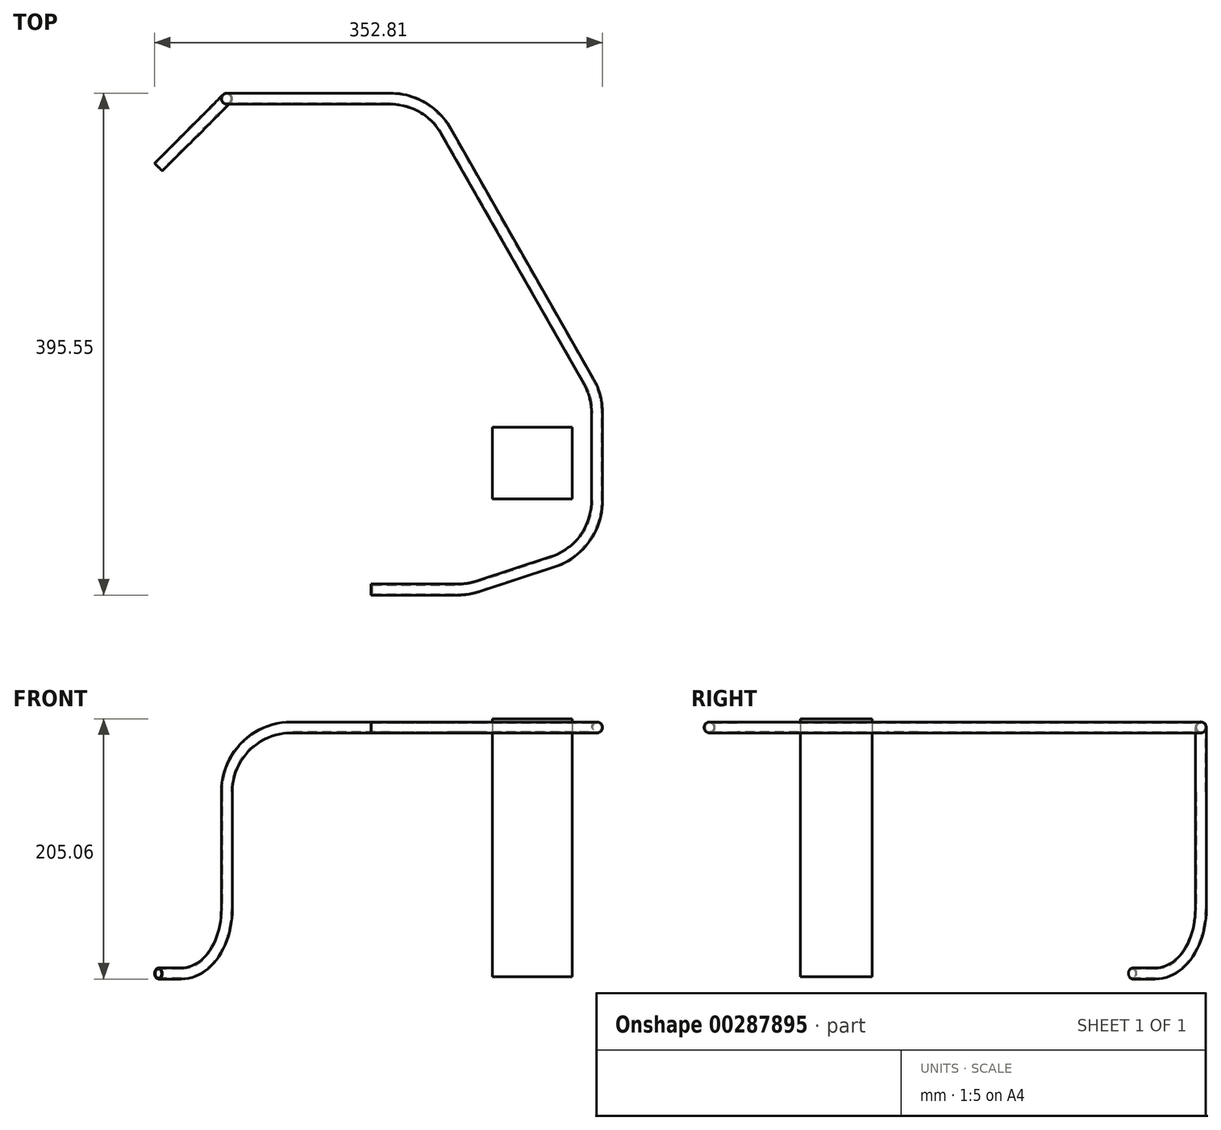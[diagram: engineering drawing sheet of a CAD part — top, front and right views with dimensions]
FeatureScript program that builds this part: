
annotation { "Feature Type Name" : "Feature", "Feature Type Description" : "" }
export const myFeature = defineFeature(function(context is Context, id is Id, definition is map)
    precondition{}
    {
        {
            var Q0;
            Q0=qCreatedBy(makeId("Top.planeOp"),FACE);
            var sketch = newSketch(context, id + "F0", { "sketchPlane" : qUnion([Q0])});
            skLineSegment(sketch, "E0", {"start": v(0, 0) * mm, "end": v(308.08, 0) * mm});
            skLineSegment(sketch, "E1", {"start": v(308.08, 0) * mm, "end": v(308.08, -99.9) * mm});
            skLineSegment(sketch, "E2", {"start": v(308.08, -99.9) * mm, "end": v(333.48, -99.9) * mm});
            skLineSegment(sketch, "E3", {"start": v(0, 0) * mm, "end": v(140.48, 0) * mm});
            skLineSegment(sketch, "E4", {"start": v(140.48, 0) * mm, "end": v(140.48, 233.1) * mm});
            skLineSegment(sketch, "E5", {"start": v(140.48, 233.1) * mm, "end": v(165.88, 233.1) * mm});
            skLineSegment(sketch, "E6", {"start": v(0, 0) * mm, "end": v(466.34, 0) * mm});
            skLineSegment(sketch, "E7", {"start": v(466.34, 0) * mm, "end": v(466.34, -28.43) * mm});
            skLineSegment(sketch, "E8", {"start": v(466.34, -28.43) * mm, "end": v(491.74, -28.43) * mm});
            skLineSegment(sketch, "E9", {"start": v(0, 0) * mm, "end": v(403.6, 0) * mm});
            skLineSegment(sketch, "E10", {"start": v(403.6, 0) * mm, "end": v(403.6, 27.96) * mm});
            skLineSegment(sketch, "E11", {"start": v(403.6, 27.96) * mm, "end": v(429, 27.96) * mm});
            skSolve(sketch);
        }
        {
            var Q0;
            Q0=sQuery(id+"F0.wireOp",EDGE,"E2");
            cPlane(context, id + "F1", {"entities" : qUnion([Q0]), "cplaneType" : CPlaneType.LINE_ANGLE, "offset" : 25.4 * mm, "angle" : 0 * degree, "width" : 152.4 * mm, "height" : 152.4 * mm});
        }
        {
            var Q0;
            Q0=sQuery(id+"F0.wireOp",EDGE,"E8");
            cPlane(context, id + "F2", {"entities" : qUnion([Q0]), "cplaneType" : CPlaneType.LINE_ANGLE, "offset" : 25.4 * mm, "angle" : 0 * degree, "width" : 152.4 * mm, "height" : 152.4 * mm});
        }
        {
            var Q0;
            Q0=sQuery(id+"F0.wireOp",EDGE,"E11");
            cPlane(context, id + "F3", {"entities" : qUnion([Q0]), "cplaneType" : CPlaneType.LINE_ANGLE, "offset" : 25.4 * mm, "angle" : 0 * degree, "width" : 152.4 * mm, "height" : 152.4 * mm});
        }
        {
            var Q0;
            Q0=sQuery(id+"F0.wireOp",EDGE,"E5");
            cPlane(context, id + "F4", {"entities" : qUnion([Q0]), "cplaneType" : CPlaneType.LINE_ANGLE, "offset" : 25.4 * mm, "angle" : 0 * degree, "width" : 152.4 * mm, "height" : 152.4 * mm});
        }
        {
            var Q0;
            Q0=qCreatedBy(id+"F2.planeOp",FACE);
            var sketch = newSketch(context, id + "F5", { "sketchPlane" : qUnion([Q0])});
            skLineSegment(sketch, "E12", {"start": v(-466.34, 0) * mm, "end": v(-466.34, 772.24) * mm});
            skLineSegment(sketch, "E13", {"start": v(-466.34, 772.24) * mm, "end": v(-440.94, 772.24) * mm});
            skSolve(sketch);
        }
        {
            var Q0;
            Q0=qCreatedBy(id+"F3.planeOp",FACE);
            var sketch = newSketch(context, id + "F6", { "sketchPlane" : qUnion([Q0])});
            skLineSegment(sketch, "E14", {"start": v(-403.6, 0) * mm, "end": v(-403.6, 772.24) * mm});
            skLineSegment(sketch, "E15", {"start": v(-403.6, 772.24) * mm, "end": v(-378.2, 772.24) * mm});
            skSolve(sketch);
        }
        {
            var Q0;
            Q0=qCreatedBy(id+"F1.planeOp",FACE);
            var sketch = newSketch(context, id + "F7", { "sketchPlane" : qUnion([Q0])});
            skLineSegment(sketch, "E16", {"start": v(-308.08, 0) * mm, "end": v(-308.08, 968.64) * mm});
            skLineSegment(sketch, "E17", {"start": v(-308.08, 968.64) * mm, "end": v(-333.48, 968.64) * mm});
            skSolve(sketch);
        }
        {
            var Q0;
            Q0=qCreatedBy(id+"F4.planeOp",FACE);
            var sketch = newSketch(context, id + "F8", { "sketchPlane" : qUnion([Q0])});
            skLineSegment(sketch, "E18", {"start": v(-140.48, 0) * mm, "end": v(-140.48, 774.72) * mm});
            skLineSegment(sketch, "E19", {"start": v(-140.48, 774.72) * mm, "end": v(-115.08, 774.72) * mm});
            skSolve(sketch);
        }
        {
            var Q0;
            Q0=sQuery(id+"F5.wireOp",EDGE,"E13");
            cPlane(context, id + "F9", {"entities" : qUnion([Q0]), "cplaneType" : CPlaneType.LINE_ANGLE, "offset" : 25.4 * mm, "angle" : 90 * degree, "width" : 152.4 * mm, "height" : 152.4 * mm});
        }
        {
            var Q0;
            Q0=qCreatedBy(id+"F9.planeOp",FACE);
            var sketch = newSketch(context, id + "F10", { "sketchPlane" : qUnion([Q0])});
            skLineSegment(sketch, "E20.bottom", {"start": v(466.34, -28.43) * mm, "end": v(403.6, -28.43) * mm});
            skLineSegment(sketch, "E20.top", {"start": v(466.34, 27.96) * mm, "end": v(403.6, 27.96) * mm});
            skLineSegment(sketch, "E20.left", {"start": v(466.34, -28.43) * mm, "end": v(466.34, 27.96) * mm});
            skLineSegment(sketch, "E20.right", {"start": v(403.6, -28.43) * mm, "end": v(403.6, 27.96) * mm});
            skSolve(sketch);
        }
        {
            var Q0;
            Q0=qSketchRegion(id+"F10",true);
            extrude(context, id + "F11", {"entities" : qUnion([Q0]), "depth" : 203.2 * mm});
        }
        {
            var Q0;
            Q0=sQuery(id+"F8.wireOp",EDGE,"E19");
            cPlane(context, id + "F12", {"entities" : qUnion([Q0]), "cplaneType" : CPlaneType.LINE_ANGLE, "offset" : 25.4 * mm, "angle" : 90 * degree, "width" : 152.4 * mm, "height" : 152.4 * mm});
        }
        {
            var Q0;
            Q0=qCreatedBy(id+"F12.planeOp",FACE);
            var sketch = newSketch(context, id + "F13", { "sketchPlane" : qUnion([Q0])});
            skLineSegment(sketch, "E21", {"start": v(140.48, 233.1) * mm, "end": v(73.87, 299.7) * mm});
            skSolve(sketch);
        }
        {
            var Q0;
            Q0=sQuery(id+"F13.wireOp",EDGE,"E21");
            cPlane(context, id + "F14", {"entities" : qUnion([Q0]), "cplaneType" : CPlaneType.LINE_ANGLE, "offset" : 25.4 * mm, "angle" : 90 * degree, "width" : 152.4 * mm, "height" : 152.4 * mm});
        }
        {
            var Q0;
            Q0=qCreatedBy(id+"F14.planeOp",FACE);
            var sketch = newSketch(context, id + "F15", { "sketchPlane" : qUnion([Q0])});
            skCircle(sketch, "E22", {"center": v(65.5, 774.72) * mm, "radius": 4.34 * mm});
            skSolve(sketch);
        }
        {
            var Q0;
            Q0=sQuery(id+"F7.wireOp",EDGE,"E16");
            cPlane(context, id + "F16", {"entities" : qUnion([Q0]), "cplaneType" : CPlaneType.LINE_ANGLE, "offset" : 25.4 * mm, "angle" : 0 * degree, "width" : 152.4 * mm, "height" : 152.4 * mm});
        }
        {
            var Q0;
            Q0=qCreatedBy(id+"F16.planeOp",FACE);
            var sketch = newSketch(context, id + "F17", { "sketchPlane" : qUnion([Q0])});
            skCircle(sketch, "E23", {"center": v(-99.9, 968.64) * mm, "radius": 4.34 * mm});
            skSolve(sketch);
        }
        {
            var Q0;
            Q0=qCreatedBy(id+"F12.planeOp",FACE);
            var sketch = newSketch(context, id + "F18", { "sketchPlane" : qUnion([Q0])});
            skLineSegment(sketch, "E24", {"start": v(140.48, 233.1) * mm, "end": v(194.36, 286.98) * mm});
            skSolve(sketch);
        }
        {
            var Q0;
            Q0=sQuery(id+"F7.wireOp",EDGE,"E17");
            cPlane(context, id + "F19", {"entities" : qUnion([Q0]), "cplaneType" : CPlaneType.LINE_ANGLE, "offset" : 25.4 * mm, "angle" : 90 * degree, "width" : 152.4 * mm, "height" : 152.4 * mm});
        }
        {
            var Q0;
            Q0=qCreatedBy(id+"F19.planeOp",FACE);
            var sketch = newSketch(context, id + "F20", { "sketchPlane" : qUnion([Q0])});
            skLineSegment(sketch, "E25", {"start": v(308.08, -99.9) * mm, "end": v(384.28, -99.9) * mm});
            skLineSegment(sketch, "E26", {"start": v(384.28, -99.9) * mm, "end": v(450.86, -78.14) * mm});
            skLineSegment(sketch, "E27", {"start": v(485.88, -29.85) * mm, "end": v(485.88, 39.28) * mm});
            skLineSegment(sketch, "E28", {"start": v(479.22, 64.43) * mm, "end": v(367.05, 261.33) * mm});
            skLineSegment(sketch, "E29", {"start": v(322.91, 286.98) * mm, "end": v(194.36, 286.98) * mm});
            skLineSegment(sketch, "E30", {"start": v(384.28, -99.9) * mm, "end": v(384.28, -66.7) * mm});
            skLineSegment(sketch, "E31", {"start": v(384.28, -66.7) * mm, "end": v(485.88, -66.7) * mm});
            skPoint(sketch, "E32.visualSharp", {"position": v(485.88, -66.7) * mm});
            skArc(sketch, "E32.filletArc", {"start": v(450.86, -78.14) * mm, "mid": v(476.2, -59.67) * mm, "end": v(485.88, -29.85) * mm});
            skPoint(sketch, "E33.visualSharp", {"position": v(485.88, 52.74) * mm});
            skArc(sketch, "E33.filletArc", {"start": v(485.88, 39.28) * mm, "mid": v(484.2, 52.3) * mm, "end": v(479.22, 64.43) * mm});
            skPoint(sketch, "E34.visualSharp", {"position": v(352.44, 286.98) * mm});
            skArc(sketch, "E34.filletArc", {"start": v(367.05, 261.33) * mm, "mid": v(348.44, 280.1) * mm, "end": v(322.91, 286.98) * mm});
            skSolve(sketch);
        }
        {
            var Q0;
            Q0=sQuery(id+"F20.wireOp",VERTEX,"E29.start");
            var Q1;
            Q1=sQuery(id+"F20.wireOp",VERTEX,"E29.end");
            var Q2;
            Q2=sQuery(id+"F18.wireOp",VERTEX,"E24.end");
            cPlane(context, id + "F21", {"entities" : qUnion([Q0, Q1, Q2]), "cplaneType" : CPlaneType.THREE_POINT, "offset" : 25.4 * mm, "width" : 152.4 * mm, "height" : 152.4 * mm});
        }
        {
            var Q0;
            Q0=qCreatedBy(id+"F21.planeOp",FACE);
            var sketch = newSketch(context, id + "F22", { "sketchPlane" : qUnion([Q0])});
            skLineSegment(sketch, "E35", {"start": v(-245.16, 968.64) * mm, "end": v(-322.91, 968.64) * mm});
            skLineSegment(sketch, "E36", {"start": v(-194.36, 917.84) * mm, "end": v(-194.36, 774.72) * mm});
            skPoint(sketch, "E37.visualSharp", {"position": v(-194.36, 968.64) * mm});
            skArc(sketch, "E37.filletArc", {"start": v(-194.36, 917.84) * mm, "mid": v(-209.24, 953.77) * mm, "end": v(-245.16, 968.64) * mm});
            skSolve(sketch);
        }
        {
            var Q0;
            Q0=sQuery(id+"F18.wireOp",EDGE,"E24");
            var Q1;
            Q1=sQuery(id+"F22.wireOp",EDGE,"E36");
            cPlane(context, id + "F23", {"entities" : qUnion([Q0, Q1]), "cplaneType" : CPlaneType.LINE_ANGLE, "offset" : 25.4 * mm, "angle" : 0 * degree, "width" : 152.4 * mm, "height" : 152.4 * mm});
        }
        {
            var Q0;
            Q0=qCreatedBy(id+"F23.planeOp",FACE);
            var sketch = newSketch(context, id + "F24", { "sketchPlane" : qUnion([Q0])});
            skLineSegment(sketch, "E38", {"start": v(-264.16, 774.72) * mm, "end": v(-289.56, 774.72) * mm});
            skLineSegment(sketch, "E39", {"start": v(-340.36, 825.52) * mm, "end": v(-340.36, 917.84) * mm});
            skPoint(sketch, "E40.visualSharp", {"position": v(-340.36, 774.72) * mm});
            skArc(sketch, "E40.filletArc", {"start": v(-340.36, 825.52) * mm, "mid": v(-325.48, 789.6) * mm, "end": v(-289.56, 774.72) * mm});
            skSolve(sketch);
        }
        {
            var Q0;
            Q0=sQuery(id+"F20.wireOp",EDGE,"E26");
            var Q1;
            Q1=sQuery(id+"F20.wireOp",EDGE,"E25");
            cPlane(context, id + "F25", {"entities" : qUnion([Q0, Q1]), "cplaneType" : CPlaneType.LINE_ANGLE, "offset" : 25.4 * mm, "angle" : 0 * degree, "width" : 152.4 * mm, "height" : 152.4 * mm});
        }
        {
            var Q0;
            Q0=qCreatedBy(id+"F25.planeOp",FACE);
            var sketch = newSketch(context, id + "F26", { "sketchPlane" : qUnion([Q0])});
            skLineSegment(sketch, "E41", {"start": v(376.2, 99.9) * mm, "end": v(308.08, 99.9) * mm});
            skLineSegment(sketch, "E42", {"start": v(391.97, 97.38) * mm, "end": v(450.86, 78.14) * mm});
            skPoint(sketch, "E43.visualSharp", {"position": v(384.28, 99.9) * mm});
            skArc(sketch, "E43.filletArc", {"start": v(391.97, 97.38) * mm, "mid": v(384.18, 99.26) * mm, "end": v(376.2, 99.9) * mm});
            skSolve(sketch);
        }
        {
            var Q0;
            Q0=makeQuery(id+"F17.imprint","IMPRINT",FACE,{"disambiguationData":[TD([[makeQuery(id+"F17.imprint","IMPRINT",EDGE,{"derivedFrom":sQuery(id+"F17.wireOp",EDGE,"E23")}),1.0]])]});
            var Q1;
            Q1=sQuery(id+"F26.wireOp",EDGE,"E41");
            var Q2;
            Q2=sQuery(id+"F26.wireOp",EDGE,"E43.filletArc");
            var Q3;
            Q3=sQuery(id+"F26.wireOp",EDGE,"E42");
            var Q4;
            Q4=sQuery(id+"F20.wireOp",EDGE,"E32.filletArc");
            var Q5;
            Q5=sQuery(id+"F20.wireOp",EDGE,"E27");
            var Q6;
            Q6=sQuery(id+"F20.wireOp",EDGE,"E33.filletArc");
            var Q7;
            Q7=sQuery(id+"F20.wireOp",EDGE,"E28");
            var Q8;
            Q8=sQuery(id+"F20.wireOp",EDGE,"E34.filletArc");
            var Q9;
            Q9=sQuery(id+"F22.wireOp",EDGE,"E35");
            var Q10;
            Q10=sQuery(id+"F22.wireOp",EDGE,"E37.filletArc");
            var Q11;
            Q11=sQuery(id+"F24.wireOp",EDGE,"E39");
            var Q12;
            Q12=sQuery(id+"F24.wireOp",EDGE,"E40.filletArc");
            var Q13;
            Q13=sQuery(id+"F24.wireOp",EDGE,"E38");
            sweep(context, id + "F27", {"profiles" : qUnion([Q0]), "path" : qUnion([Q1, Q2, Q3, Q4, Q5, Q6, Q7, Q8, Q9, Q10, Q11, Q12, Q13])});
        }
        {
            var Q0;
            Q0=makeQuery(id+"F27.opSweep","CAP_FACE",FACE,{"disambiguationData":[OSD([sQuery(id+"F17.wireOp",EDGE,"E23"),sQuery(id+"F24.wireOp",VERTEX,"E38.start")])],"isStart":false});
            shell(context, id + "F28", {"entities" : qUnion([Q0]), "thickness" : 0.76 * mm});
        }
    });
